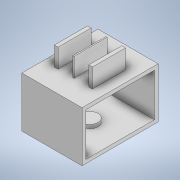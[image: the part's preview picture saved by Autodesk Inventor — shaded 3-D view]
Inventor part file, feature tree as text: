
AUTODESK INVENTOR PART (.ipt)
format: ipt  version: 2020 (Build 240168000, 168)  size: 190,976 bytes
history: native  units: mm
features: extrude x7, sketch x7
ambient origin geometry x8: Origin, YZ Plane, XZ Plane, XY Plane, X Axis, Y Axis, Z Axis, Center Point
bodies: Solid1 (feature_tree)
feature tree (14):
  extrude  "Extrusion1"  Depth=12.0mm
  extrude  "Extrusion2"  Depth=27.0mm
  extrude  "Extrusion3"  TaperAngle=0.0deg  [1 undecoded]
  extrude  "Extrusion4"  Depth=13.5mm
  extrude  "Extrusion7"  Depth=3.0mm
  extrude  "Extrusion8"  TaperAngle=0.0deg  [1 undecoded]
  extrude  "Extrusion9"  Depth=56.0mm
  sketch  "Sketch1"  dims[d0=12.0mm d1=12.0mm]
  sketch  "Sketch2"  dims[d2=1.0mm d3=27.0mm]
  sketch  "Sketch7"  dims[d8=3.0mm d9=3.0mm]
  sketch  "Sketch8"  dims[d10=0.0mm d11=0.0mm]
  sketch  "Sketch9"  dims[d12=15.5mm d13=0.0mm d14=56.0mm d15=28.0mm d16=9.0mm d17=9.0mm d18=3.0mm d19=3.0mm d20=3.0mm d21=0.0mm d22=56.0mm d23=28.0mm d26=3.0mm d27=3.0mm d28=35.0mm d29=0.0mm d30=56.0mm d31=28.0mm d34=3.0mm d35=3.0mm d36=3.0mm d37=0.0mm d45=13.0mm d46=6.0mm d47=0.0mm d48=7.5mm d49=10.0mm d50=5.0mm d51=0.0mm d52=13.0mm d53=10.0mm d54=7.5mm d55=5.0mm d56=0.0mm]
  sketch  "Sketch3"  dims[d4=27.0mm d5=0.0mm]
  sketch  "Sketch4"  dims[d6=0.5mm d7=13.5mm]
note: 2 required parameter values undecoded (feature->parameter linkage not recoverable at this tier; creation-order binding heuristic only, values carry confidence <= 0.55)
